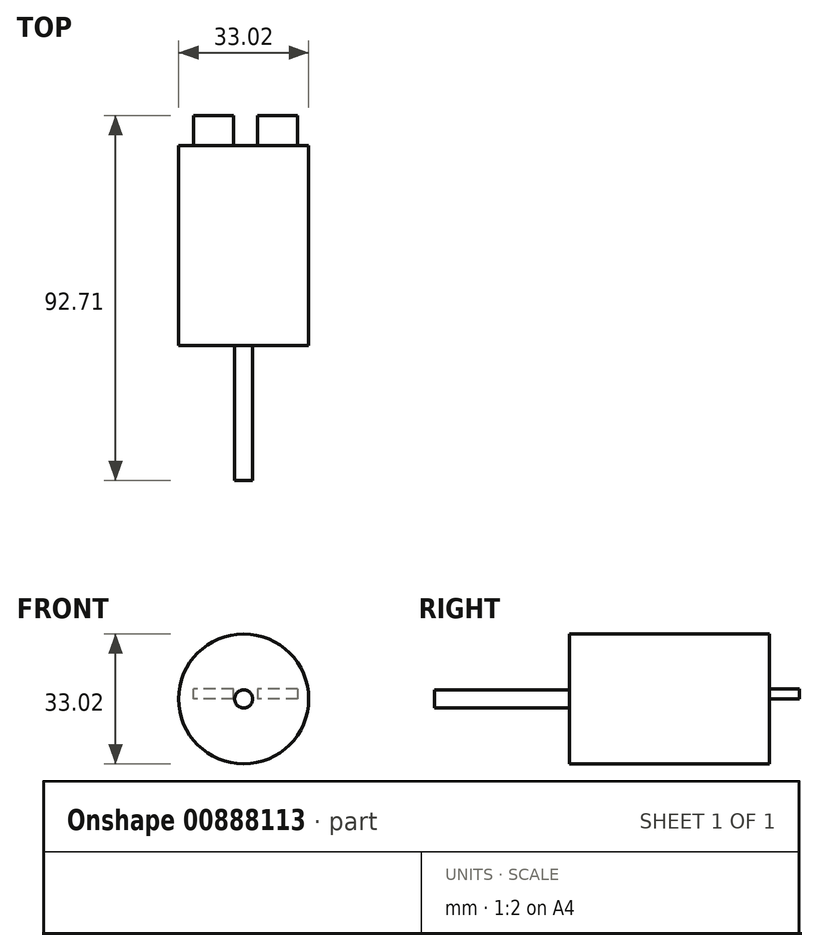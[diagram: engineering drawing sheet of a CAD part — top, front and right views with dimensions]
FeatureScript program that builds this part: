
annotation { "Feature Type Name" : "Feature", "Feature Type Description" : "" }
export const myFeature = defineFeature(function(context is Context, id is Id, definition is map)
    precondition{}
    {
        {
            var Q0;
            Q0=qCreatedBy(makeId("Front.planeOp"),FACE);
            var sketch = newSketch(context, id + "F0", { "sketchPlane" : qUnion([Q0])});
            skCircle(sketch, "E0", {"center": v(0, 0) * mm, "radius": 16.51 * mm});
            skSolve(sketch);
        }
        {
            var Q0;
            Q0 = qSketchRegion(id + "F0", true);
            extrude(context, id + "F1", {"entities" : qUnion([Q0]), "depth" : 50.8 * mm, "offsetDistance" : 25.4 * mm});
        }
        {
            var Q0;
            Q0=makeQuery(id+"F1.opExtrude","CAP_FACE",FACE,{"disambiguationData":[OSD([sQuery(id+"F0.wireOp",EDGE,"E0")])],"isStart":false});
            var sketch = newSketch(context, id + "F2", { "sketchPlane" : qUnion([Q0])});
            skCircle(sketch, "E1", {"center": v(0, 0) * mm, "radius": 2.29 * mm});
            skSolve(sketch);
        }
        {
            var Q0;
            Q0=makeQuery(id+"F2.imprint","IMPRINT",FACE,{"disambiguationData":[TD([[makeQuery(id+"F2.imprint","IMPRINT",EDGE,{"derivedFrom":sQuery(id+"F2.wireOp",EDGE,"E1")}),1.0]])]});
            extrude(context, id + "F3", {"entities" : qUnion([Q0]), "operationType" : NewBodyOperationType.ADD, "depth" : 34.3 * mm, "offsetDistance" : 25.4 * mm});
        }
        {
            var Q0;
            Q0=makeQuery(id+"F1.opExtrude","CAP_FACE",FACE,{"disambiguationData":[OSD([sQuery(id+"F0.wireOp",EDGE,"E0")])],"isStart":true});
            var sketch = newSketch(context, id + "F4", { "sketchPlane" : qUnion([Q0])});
            skLineSegment(sketch, "E2.bottom", {"start": v(-13.74, 2.54) * mm, "end": v(-3.58, 2.54) * mm});
            skLineSegment(sketch, "E2.top", {"start": v(-13.74, 0) * mm, "end": v(-3.58, 0) * mm});
            skLineSegment(sketch, "E2.left", {"start": v(-13.74, 2.54) * mm, "end": v(-13.74, 0) * mm});
            skLineSegment(sketch, "E2.right", {"start": v(-3.58, 2.54) * mm, "end": v(-3.58, 0) * mm});
            skLineSegment(sketch, "E3.bottom", {"start": v(2.57, 0) * mm, "end": v(12.73, 0) * mm});
            skLineSegment(sketch, "E3.top", {"start": v(2.57, 2.54) * mm, "end": v(12.73, 2.54) * mm});
            skLineSegment(sketch, "E3.left", {"start": v(2.57, 0) * mm, "end": v(2.57, 2.54) * mm});
            skLineSegment(sketch, "E3.right", {"start": v(12.73, 0) * mm, "end": v(12.73, 2.54) * mm});
            skSolve(sketch);
        }
        {
            var Q0;
            Q0 = qSketchRegion(id + "F4", true);
            extrude(context, id + "F5", {"entities" : qUnion([Q0]), "operationType" : NewBodyOperationType.ADD, "depth" : 7.62 * mm, "offsetDistance" : 25.4 * mm});
        }
    });
